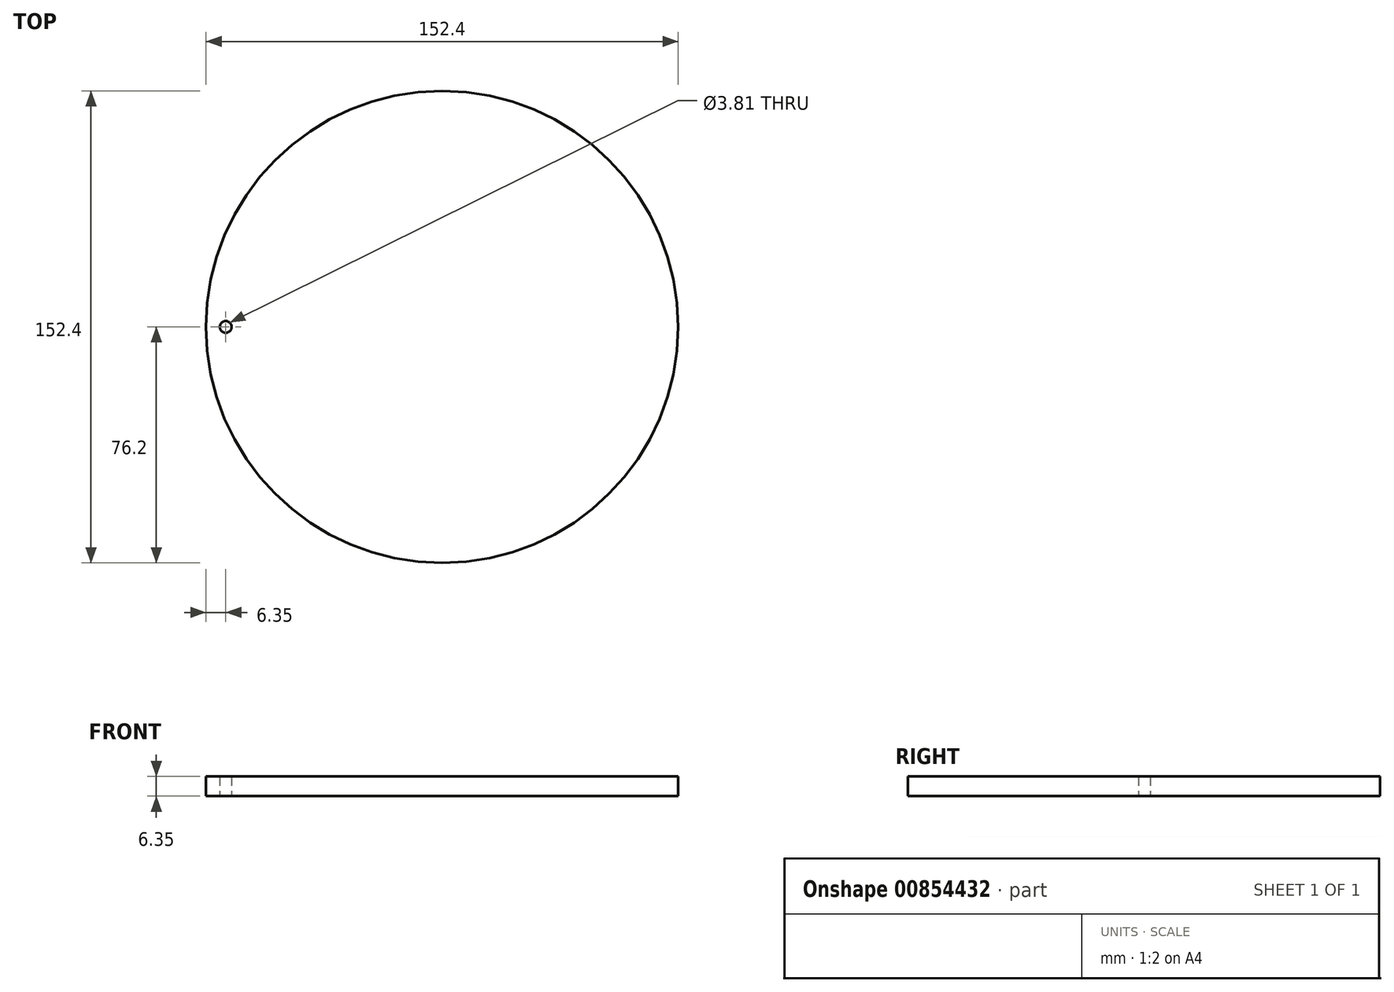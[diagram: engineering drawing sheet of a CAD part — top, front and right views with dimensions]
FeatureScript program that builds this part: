
annotation { "Feature Type Name" : "Feature", "Feature Type Description" : "" }
export const myFeature = defineFeature(function(context is Context, id is Id, definition is map)
    precondition{}
    {
        {
            var Q0;
            Q0=qCreatedBy(makeId("Top.planeOp"),FACE);
            var sketch = newSketch(context, id + "F0", { "sketchPlane" : qUnion([Q0])});
            skCircle(sketch, "E0", {"center": v(0, 0) * mm, "radius": 76.2 * mm});
            skLineSegment(sketch, "E1", {"start": v(-76.2, 0) * mm, "end": v(76.2, 0) * mm, "construction": true});
            skCircle(sketch, "E2", {"center": v(-69.85, 0) * mm, "radius": 1.9 * mm});
            skSolve(sketch);
        }
        {
            var Q0;
            Q0=makeQuery(id+"F0.imprint","IMPRINT",FACE,{"disambiguationData":[TD([[makeQuery(id+"F0.imprint","IMPRINT",EDGE,{"derivedFrom":sQuery(id+"F0.wireOp",EDGE,"E0")}),1.0]])]});
            var Q1;
            Q1=sQuery(id+"F0.wireOp",EDGE,"E0");
            var Q2;
            Q2=sQuery(id+"F0.wireOp",EDGE,"E2");
            extrude(context, id + "F1", {"entities" : qUnion([Q0]), "surfaceEntities" : qUnion([Q1, Q2]), "depth" : 6.35 * mm, "offsetDistance" : 25.4 * mm});
        }
    });
